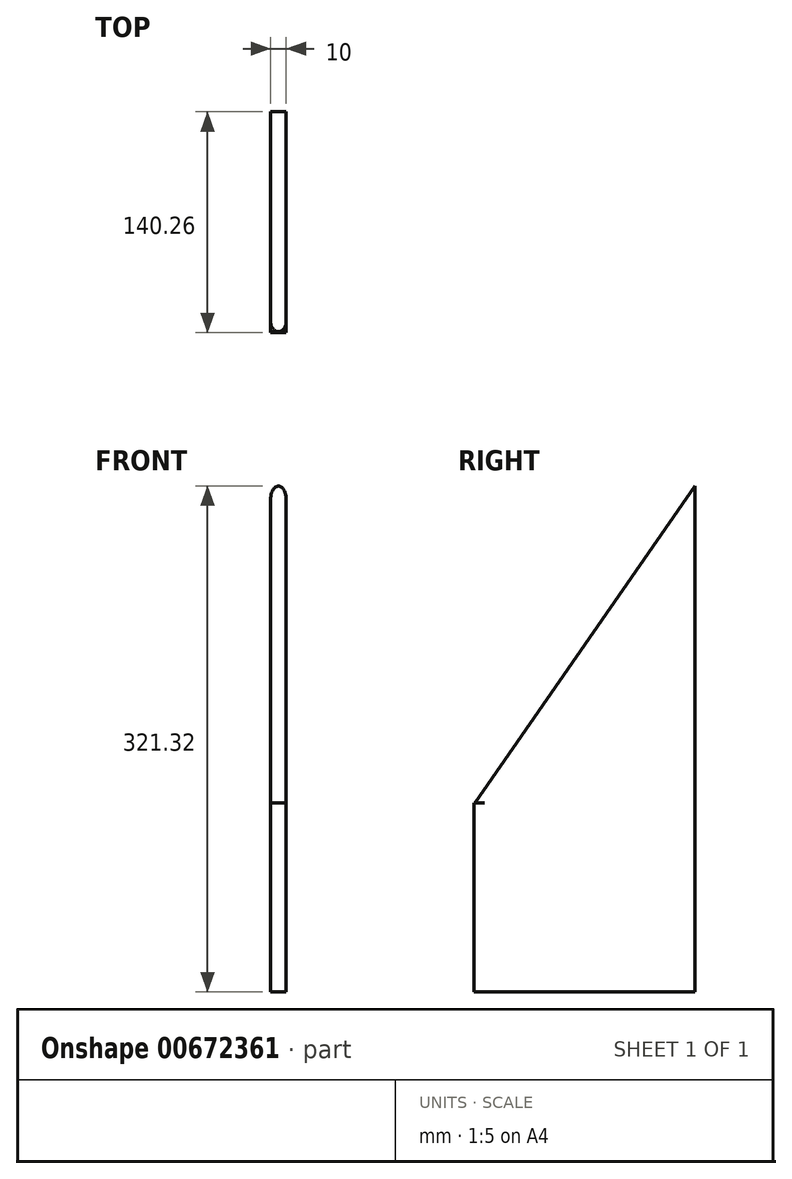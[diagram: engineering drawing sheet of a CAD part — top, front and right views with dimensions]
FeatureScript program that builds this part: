
annotation { "Feature Type Name" : "Feature", "Feature Type Description" : "" }
export const myFeature = defineFeature(function(context is Context, id is Id, definition is map)
    precondition{}
    {
        {
            var Q0;
            Q0=qCreatedBy(makeId("Right.planeOp"),FACE);
            var sketch = newSketch(context, id + "F0", { "sketchPlane" : qUnion([Q0])});
            skLineSegment(sketch, "E0.bottom", {"start": v(-140.26, 0) * mm, "end": v(-139.63, 0) * mm});
            skLineSegment(sketch, "E0.top", {"start": v(-140.26, 120) * mm, "end": v(-139.63, 120) * mm});
            skLineSegment(sketch, "E0.left", {"start": v(-139.63, 0) * mm, "end": v(-139.63, 120) * mm});
            skLineSegment(sketch, "E0.right", {"start": v(-140.26, 0) * mm, "end": v(-140.26, 120) * mm});
            skLineSegment(sketch, "E1.bottom", {"start": v(0, 0) * mm, "end": v(0, 0) * mm});
            skLineSegment(sketch, "E1.top", {"start": v(0, 321.32) * mm, "end": v(0, 321.32) * mm});
            skLineSegment(sketch, "E1.left", {"start": v(0, 0) * mm, "end": v(0, 321.32) * mm});
            skLineSegment(sketch, "E1.right", {"start": v(0, 0) * mm, "end": v(0, 321.32) * mm});
            skLineSegment(sketch, "E2", {"start": v(0, 321.32) * mm, "end": v(-139.63, 120) * mm});
            skLineSegment(sketch, "E3", {"start": v(-140.26, 0) * mm, "end": v(0, 0) * mm});
            skSolve(sketch);
        }
        {
            var Q0;
            Q0=qSketchRegion(id+"F0",true);
            extrude(context, id + "F1", {"entities" : qUnion([Q0]), "depth" : 10 * mm, "offsetDistance" : 25 * mm});
        }
        {
            var Q0;
            Q0=makeQuery(id+"F1.opExtrude","CAP_EDGE",EDGE,{"disambiguationData":[OSD([sQuery(id+"F0.wireOp",EDGE,"E2")])],"isStart":false});
            var Q1;
            Q1=makeQuery(id+"F1.opExtrude","CAP_EDGE",EDGE,{"disambiguationData":[OSD([sQuery(id+"F0.wireOp",EDGE,"E2")])],"isStart":true});
            fillet(context, id + "F2", {"entities" : qUnion([Q0, Q1]), "radius" : 5 * mm, "tangentPropagation" : true, "allowEdgeOverflow" : false});
        }
    });
